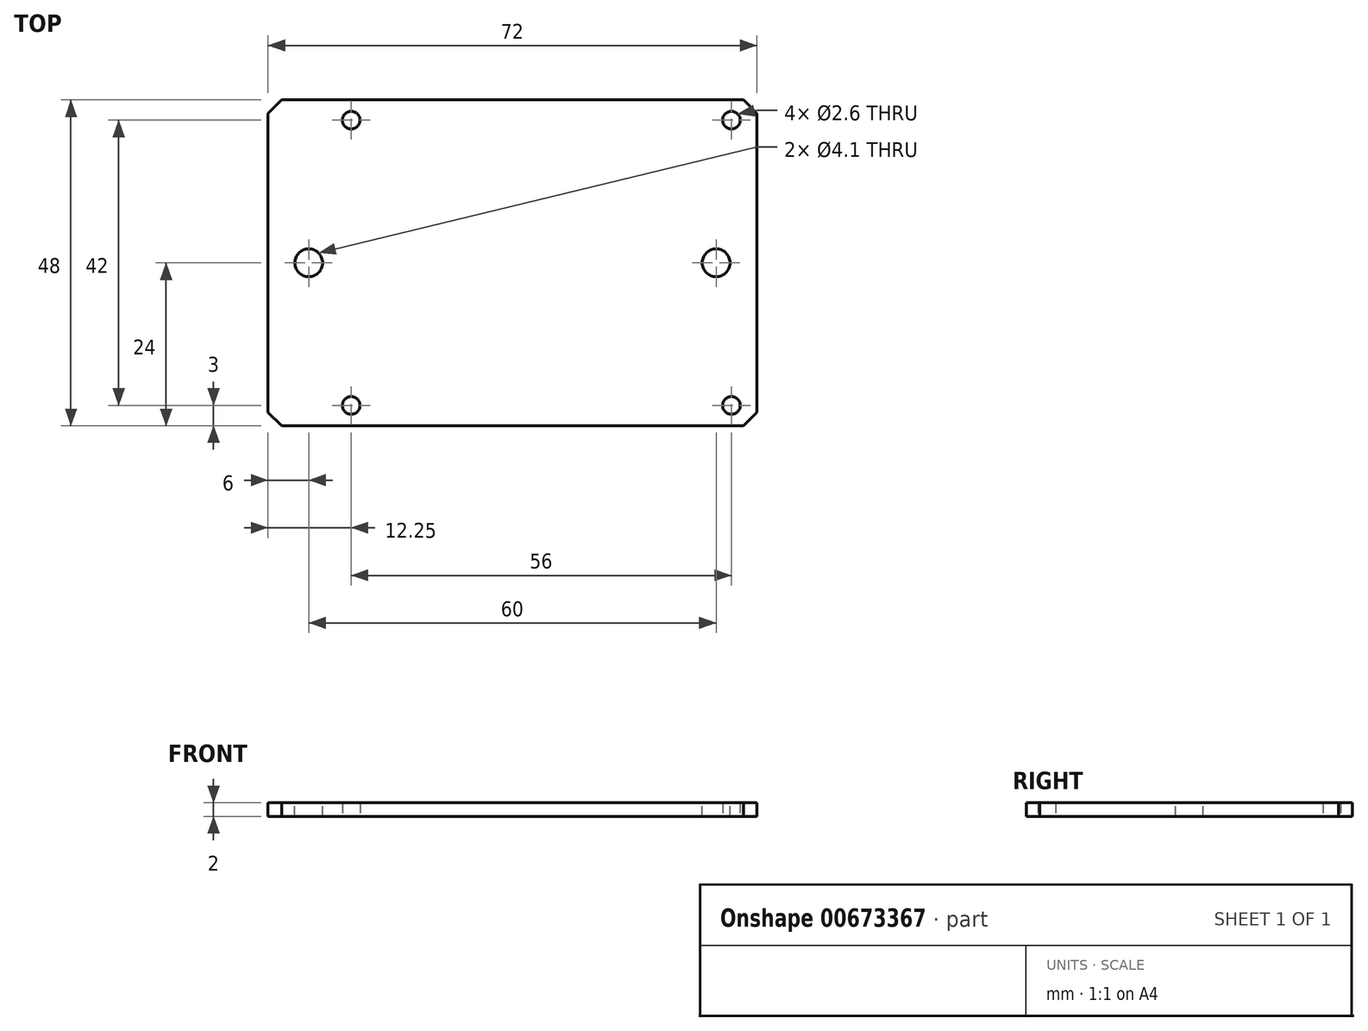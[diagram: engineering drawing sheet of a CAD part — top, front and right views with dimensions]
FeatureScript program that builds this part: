
annotation { "Feature Type Name" : "Feature", "Feature Type Description" : "" }
export const myFeature = defineFeature(function(context is Context, id is Id, definition is map)
    precondition{}
    {
        {
            var Q0;
            Q0=qCreatedBy(makeId("Top.planeOp"),FACE);
            var sketch = newSketch(context, id + "F0", { "sketchPlane" : qUnion([Q0])});
            skLineSegment(sketch, "E0.bottom", {"start": v(-36, 24) * mm, "end": v(36, 24) * mm});
            skLineSegment(sketch, "E0.top", {"start": v(-36, -24) * mm, "end": v(36, -24) * mm});
            skLineSegment(sketch, "E0.left", {"start": v(-36, 24) * mm, "end": v(-36, -24) * mm});
            skLineSegment(sketch, "E0.right", {"start": v(36, 24) * mm, "end": v(36, -24) * mm});
            skCircle(sketch, "E1", {"center": v(32.25, -21) * mm, "radius": 1.3 * mm});
            skCircle(sketch, "E2.0.1.0", {"center": v(32.25, 21) * mm, "radius": 1.3 * mm});
            skCircle(sketch, "E2.1.0.0", {"center": v(-23.75, -21) * mm, "radius": 1.3 * mm});
            skCircle(sketch, "E2.1.1.0", {"center": v(-23.75, 21) * mm, "radius": 1.3 * mm});
            skLineSegment(sketch, "E2.direction1", {"start": v(32.25, -21) * mm, "end": v(-23.75, -21) * mm, "construction": true});
            skLineSegment(sketch, "E2.direction2", {"start": v(32.25, -21) * mm, "end": v(32.25, 21) * mm, "construction": true});
            skSolve(sketch);
        }
        {
            var Q0;
            Q0 = qSketchRegion(id + "F0", true);
            extrude(context, id + "F1", {"entities" : qUnion([Q0]), "depth" : 2 * mm, "offsetDistance" : 25 * mm});
        }
        {
            var Q0;
            Q0=makeQuery(id+"F1.opExtrude","SWEPT_EDGE",EDGE,{"disambiguationData":[OSD([sQuery(id+"F0.wireOp",EDGE,"E0.top"),sQuery(id+"F0.wireOp",EDGE,"E0.left")])]});
            var Q1;
            Q1=makeQuery(id+"F1.opExtrude","SWEPT_EDGE",EDGE,{"disambiguationData":[OSD([sQuery(id+"F0.wireOp",EDGE,"E0.top"),sQuery(id+"F0.wireOp",EDGE,"E0.right")])]});
            var Q2;
            Q2=makeQuery(id+"F1.opExtrude","SWEPT_EDGE",EDGE,{"disambiguationData":[OSD([sQuery(id+"F0.wireOp",EDGE,"E0.bottom"),sQuery(id+"F0.wireOp",EDGE,"E0.right")])]});
            var Q3;
            Q3=makeQuery(id+"F1.opExtrude","SWEPT_EDGE",EDGE,{"disambiguationData":[OSD([sQuery(id+"F0.wireOp",EDGE,"E0.bottom"),sQuery(id+"F0.wireOp",EDGE,"E0.left")])]});
            chamfer(context, id + "F2", {"entities" : qUnion([Q0, Q1, Q2, Q3]), "width" : 2 * mm, "tangentPropagation" : true});
        }
        {
            var Q0;
            Q0=makeQuery(id+"F1.opExtrude","CAP_FACE",FACE,{"disambiguationData":[OSD([sQuery(id+"F0.wireOp",EDGE,"E0.bottom"),sQuery(id+"F0.wireOp",EDGE,"E0.top"),sQuery(id+"F0.wireOp",EDGE,"E0.left"),sQuery(id+"F0.wireOp",EDGE,"E0.right"),sQuery(id+"F0.wireOp",EDGE,"E1"),sQuery(id+"F0.wireOp",EDGE,"E2.0.1.0"),sQuery(id+"F0.wireOp",EDGE,"E2.1.0.0"),sQuery(id+"F0.wireOp",EDGE,"E2.1.1.0")])],"isStart":false});
            var sketch = newSketch(context, id + "F3", { "sketchPlane" : qUnion([Q0])});
            skCircle(sketch, "E3", {"center": v(-30, 0) * mm, "radius": 2.05 * mm});
            skCircle(sketch, "E4", {"center": v(30, 0) * mm, "radius": 2.05 * mm});
            skSolve(sketch);
        }
        {
            var Q0;
            Q0 = qSketchRegion(id + "F3", true);
            extrude(context, id + "F4", {"entities" : qUnion([Q0]), "operationType" : NewBodyOperationType.REMOVE, "oppositeDirection" : true, "depth" : 25 * mm, "offsetDistance" : 25 * mm});
        }
    });
